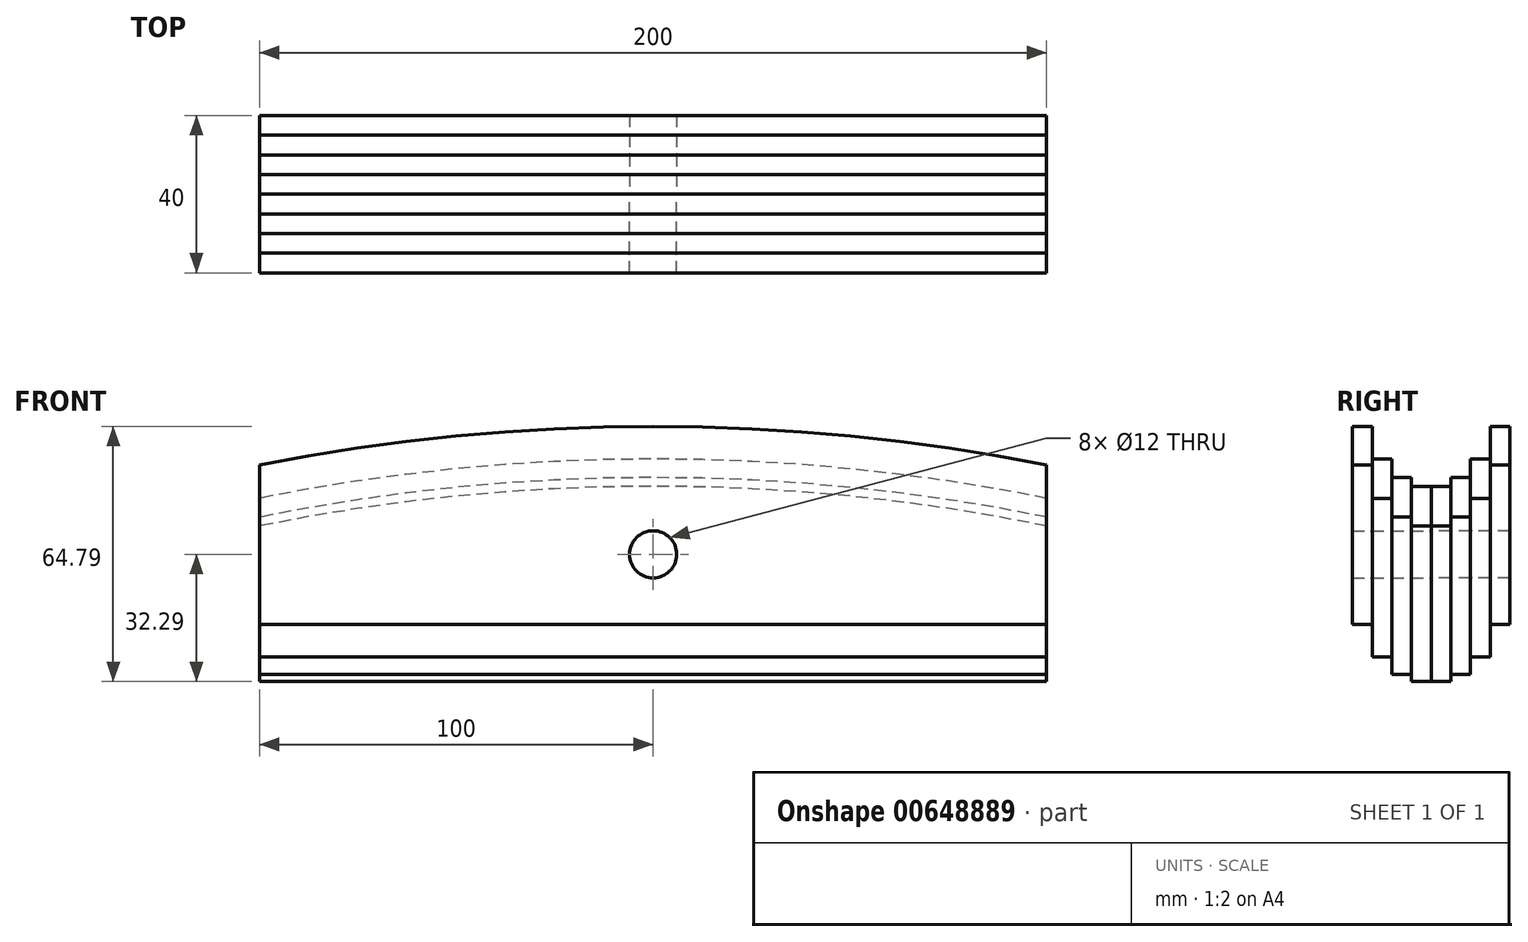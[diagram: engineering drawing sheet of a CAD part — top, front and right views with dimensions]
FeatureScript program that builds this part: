
annotation { "Feature Type Name" : "Feature", "Feature Type Description" : "" }
export const myFeature = defineFeature(function(context is Context, id is Id, definition is map)
    precondition{}
    {
        {
            var Q0;
            Q0=qCreatedBy(makeId("Front.planeOp"),FACE);
            var sketch = newSketch(context, id + "F0", { "sketchPlane" : qUnion([Q0])});
            skCircle(sketch, "E0", {"center": v(0, 0) * mm, "radius": 6 * mm});
            skLineSegment(sketch, "E1.top", {"start": v(-100, -32.3) * mm, "end": v(100, -32.3) * mm});
            skLineSegment(sketch, "E1.left", {"start": v(-100, 7.19) * mm, "end": v(-100, -32.3) * mm});
            skLineSegment(sketch, "E1.right", {"start": v(100, 7.19) * mm, "end": v(100, -32.29) * mm});
            skArc(sketch, "E2", {"start": v(-100, 7.19) * mm, "mid": v(0, 17.3) * mm, "end": v(100, 7.19) * mm});
            skSolve(sketch);
        }
        {
            var Q0;
            Q0 = qSketchRegion(id + "F0", true);
            extrude(context, id + "F1", {"entities" : qUnion([Q0]), "depth" : 5 * mm, "offsetDistance" : 25 * mm});
        }
        {
            var Q0;
            Q0=makeQuery(id+"F1.opExtrude","CAP_FACE",FACE,{"disambiguationData":[OSD([sQuery(id+"F0.wireOp",EDGE,"E0"),sQuery(id+"F0.wireOp",EDGE,"E1.top"),sQuery(id+"F0.wireOp",EDGE,"E1.left"),sQuery(id+"F0.wireOp",EDGE,"E1.right"),sQuery(id+"F0.wireOp",EDGE,"E2")])],"isStart":false});
            var sketch = newSketch(context, id + "F2", { "sketchPlane" : qUnion([Q0])});
            skLineSegment(sketch, "E3.bottom", {"start": v(100, -30.49) * mm, "end": v(-100, -30.5) * mm});
            skLineSegment(sketch, "E3.left", {"start": v(100, -30.49) * mm, "end": v(100, 9.45) * mm});
            skLineSegment(sketch, "E3.right", {"start": v(-100, -30.5) * mm, "end": v(-100, 9.45) * mm});
            skPoint(sketch, "E3.middle", {"position": v(0, -5.49) * mm});
            skArc(sketch, "E4.0", {"start": v(-100, 7.19) * mm, "mid": v(0, 17.3) * mm, "end": v(100, 7.19) * mm, "construction": true});
            skArc(sketch, "E5", {"start": v(-100, 9.45) * mm, "mid": v(0, 19.51) * mm, "end": v(100, 9.45) * mm});
            skPoint(sketch, "E6.orphan", {"position": v(-100, 19.5) * mm});
            skPoint(sketch, "E7.orphan", {"position": v(100, 19.51) * mm});
            skCircle(sketch, "E8.0", {"center": v(0, 0) * mm, "radius": 6 * mm});
            skSolve(sketch);
        }
        {
            var Q0;
            Q0 = qSketchRegion(id + "F2", true);
            extrude(context, id + "F3", {"entities" : qUnion([Q0]), "depth" : 5 * mm, "offsetDistance" : 25 * mm});
        }
        {
            var Q0;
            Q0=makeQuery(id+"F3.opExtrude","CAP_FACE",FACE,{"disambiguationData":[OSD([sQuery(id+"F2.wireOp",EDGE,"E3.bottom"),sQuery(id+"F2.wireOp",EDGE,"E3.left"),sQuery(id+"F2.wireOp",EDGE,"E3.right"),sQuery(id+"F2.wireOp",EDGE,"E5"),sQuery(id+"F2.wireOp",EDGE,"E8.0")])],"isStart":false});
            var sketch = newSketch(context, id + "F4", { "sketchPlane" : qUnion([Q0])});
            skLineSegment(sketch, "E9.bottom", {"start": v(100, -26.09) * mm, "end": v(-100, -26.1) * mm});
            skLineSegment(sketch, "E9.left", {"start": v(100, -26.09) * mm, "end": v(100, 14.25) * mm});
            skLineSegment(sketch, "E9.right", {"start": v(-100, -26.1) * mm, "end": v(-100, 14.25) * mm});
            skPoint(sketch, "E9.middle", {"position": v(0, -0.94) * mm});
            skArc(sketch, "E10.0", {"start": v(-100, 9.45) * mm, "mid": v(0, 19.51) * mm, "end": v(100, 9.45) * mm, "construction": true});
            skArc(sketch, "E11", {"start": v(-100, 14.25) * mm, "mid": v(0, 24.2) * mm, "end": v(100, 14.25) * mm});
            skCircle(sketch, "E12.0", {"center": v(0, 0) * mm, "radius": 6 * mm});
            skPoint(sketch, "E13.orphan", {"position": v(-100, 24.2) * mm});
            skPoint(sketch, "E14.orphan", {"position": v(100, 24.21) * mm});
            skSolve(sketch);
        }
        {
            var Q0;
            Q0 = qSketchRegion(id + "F4", true);
            extrude(context, id + "F5", {"entities" : qUnion([Q0]), "depth" : 5 * mm, "offsetDistance" : 25 * mm});
        }
        {
            var Q0;
            Q0=makeQuery(id+"F5.opExtrude","CAP_FACE",FACE,{"disambiguationData":[OSD([sQuery(id+"F4.wireOp",EDGE,"E9.bottom"),sQuery(id+"F4.wireOp",EDGE,"E9.left"),sQuery(id+"F4.wireOp",EDGE,"E9.right"),sQuery(id+"F4.wireOp",EDGE,"E11"),sQuery(id+"F4.wireOp",EDGE,"E12.0")])],"isStart":false});
            var sketch = newSketch(context, id + "F6", { "sketchPlane" : qUnion([Q0])});
            skLineSegment(sketch, "E15.bottom", {"start": v(100, -17.79) * mm, "end": v(-100, -17.8) * mm});
            skLineSegment(sketch, "E15.left", {"start": v(100, -17.79) * mm, "end": v(100, 22.7) * mm});
            skLineSegment(sketch, "E15.right", {"start": v(-100, -17.8) * mm, "end": v(-100, 22.7) * mm});
            skPoint(sketch, "E15.middle", {"position": v(0, 7.36) * mm});
            skArc(sketch, "E16.0", {"start": v(-100, 14.25) * mm, "mid": v(0, 24.2) * mm, "end": v(100, 14.25) * mm, "construction": true});
            skArc(sketch, "E17", {"start": v(-100, 22.7) * mm, "mid": v(0, 32.5) * mm, "end": v(100, 22.7) * mm});
            skPoint(sketch, "E18.orphan", {"position": v(-100, 32.5) * mm});
            skPoint(sketch, "E19.orphan", {"position": v(100, 32.5) * mm});
            skCircle(sketch, "E20.0", {"center": v(0, 0) * mm, "radius": 6 * mm});
            skSolve(sketch);
        }
        {
            var Q0;
            Q0 = qSketchRegion(id + "F6", true);
            extrude(context, id + "F7", {"entities" : qUnion([Q0]), "depth" : 5 * mm, "offsetDistance" : 25 * mm});
        }
        {
            var Q0;
            Q0=makeQuery(id+"F1.opExtrude","SWEPT_BODY",BODY,{"disambiguationData":[OSD([sQuery(id+"F0.wireOp",EDGE,"E0"),sQuery(id+"F0.wireOp",EDGE,"E1.top"),sQuery(id+"F0.wireOp",EDGE,"E1.left"),sQuery(id+"F0.wireOp",EDGE,"E1.right"),sQuery(id+"F0.wireOp",EDGE,"E2")])]});
            var Q1;
            Q1=makeQuery(id+"F3.opExtrude","SWEPT_BODY",BODY,{"disambiguationData":[OSD([sQuery(id+"F2.wireOp",EDGE,"E3.bottom"),sQuery(id+"F2.wireOp",EDGE,"E3.left"),sQuery(id+"F2.wireOp",EDGE,"E3.right"),sQuery(id+"F2.wireOp",EDGE,"E5"),sQuery(id+"F2.wireOp",EDGE,"E8.0")])]});
            var Q2;
            Q2=makeQuery(id+"F5.opExtrude","SWEPT_BODY",BODY,{"disambiguationData":[OSD([sQuery(id+"F4.wireOp",EDGE,"E9.bottom"),sQuery(id+"F4.wireOp",EDGE,"E9.left"),sQuery(id+"F4.wireOp",EDGE,"E9.right"),sQuery(id+"F4.wireOp",EDGE,"E11"),sQuery(id+"F4.wireOp",EDGE,"E12.0")])]});
            var Q3;
            Q3=makeQuery(id+"F7.opExtrude","SWEPT_BODY",BODY,{"disambiguationData":[OSD([sQuery(id+"F6.wireOp",EDGE,"E15.bottom"),sQuery(id+"F6.wireOp",EDGE,"E15.left"),sQuery(id+"F6.wireOp",EDGE,"E15.right"),sQuery(id+"F6.wireOp",EDGE,"E17"),sQuery(id+"F6.wireOp",EDGE,"E20.0")])]});
            var Q4;
            Q4=qCreatedBy(makeId("Front.planeOp"),FACE);
            mirror(context, id + "F8", {"entities" : qUnion([Q0, Q1, Q2, Q3]), "mirrorPlane" : qUnion([Q4])});
        }
    });
